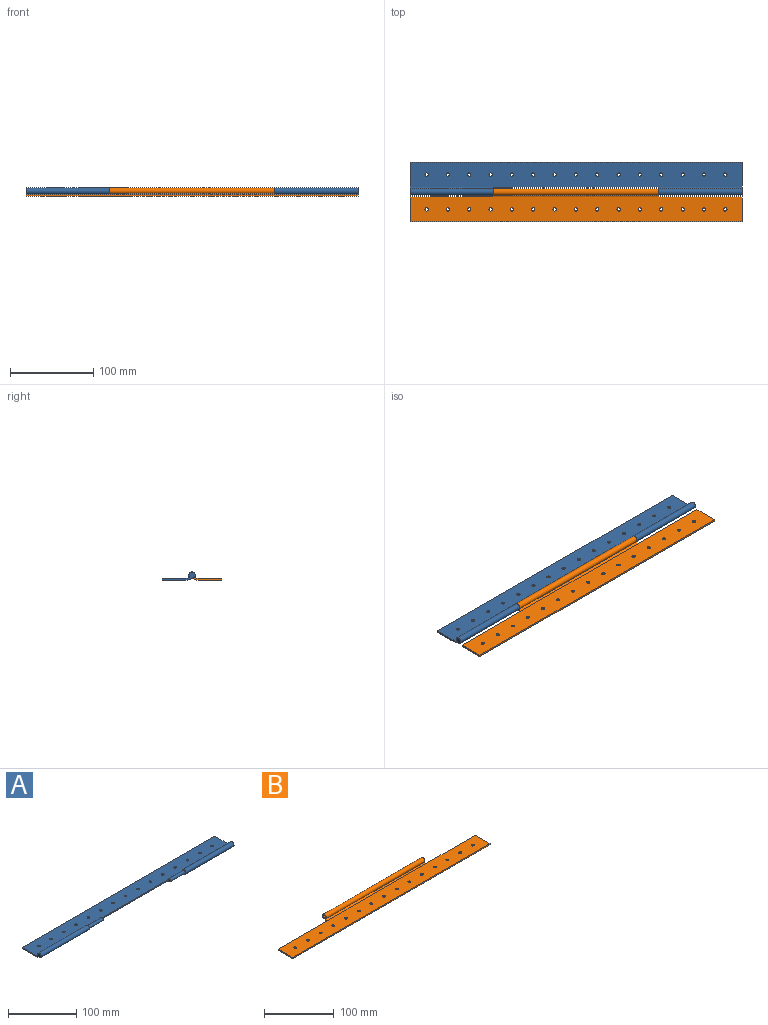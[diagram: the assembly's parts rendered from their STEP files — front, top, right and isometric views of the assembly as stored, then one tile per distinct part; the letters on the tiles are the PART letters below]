
ASSEMBLY  parts=2 mates=1
PART A: 33 faces, bbox 400x39.9x9.7 mm
  f0: cylinder r=3.86mm len=100mm, axis (1,0,0), area 2115.6mm2, adj f1,f2,f5,f6
  f1: plane 39.91x9.68mm, normal (-1,0,0), area 115.6mm2, adj f0,f5,f6,f15,f31,f32
  f2: plane 9.91x9.68mm, normal (1,0,0), area 36mm2, adj f0,f3,f5,f6,f7
  f3: cylinder r=2.5mm len=30mm, axis (-1,0,0), area 471.2mm2, adj f2,f4
  f4: plane 5x5mm, normal (1,0,0), area 19.6mm2, adj f3
  f5: plane 100x3.32mm, normal (0,0.31,0.95), area 349.9mm2, adj f0,f1,f2,f31
  f6: plane 100x6.1mm, normal (0,-0.31,-0.95), area 640.7mm2, adj f0,f1,f2,f32
  f7: plane 200x2mm, normal (0,-1,0), area 400mm2, adj f2,f9,f31,f32
  f8: cylinder r=3.86mm len=100mm, axis (1,0,0), area 2120.4mm2, adj f9,f10,f13,f14
  f9: plane 9.91x9.68mm, normal (-1,0,0), area 35.9mm2, adj f7,f8,f11,f13,f14
  f10: plane 39.91x9.68mm, normal (1,0,0), area 115.6mm2, adj f8,f13,f14,f15,f31,f32
  f11: cylinder r=2.5mm len=30mm, axis (1,0,0), area 471.2mm2, adj f9,f12
  f12: plane 5x5mm, normal (-1,0,0), area 19.6mm2, adj f11
  f13: plane 100x3.32mm, normal (0,0.31,0.95), area 349.9mm2, adj f8,f9,f10,f31
  f14: plane 100x6.05mm, normal (0,-0.31,-0.95), area 636.2mm2, adj f8,f9,f10,f32
  f15: plane 400x2mm, normal (0,1,0), area 800mm2, adj f1,f10,f31,f32
  f16: cylinder r=2mm len=4mm, axis (0,0,-1), area 25.1mm2, adj f31,f32
  f17: cylinder r=2mm len=4mm, axis (0,0,-1), area 25.1mm2, adj f31,f32
  f18: cylinder r=2mm len=4mm, axis (0,0,-1), area 25.1mm2, adj f31,f32
  f19: cylinder r=2mm len=4mm, axis (0,0,-1), area 25.1mm2, adj f31,f32
  f20: cylinder r=2mm len=4mm, axis (0,0,-1), area 25.1mm2, adj f31,f32
  f21: cylinder r=2mm len=4mm, axis (0,0,-1), area 25.1mm2, adj f31,f32
  f22: cylinder r=2mm len=4mm, axis (0,0,-1), area 25.1mm2, adj f31,f32
  f23: cylinder r=2mm len=4mm, axis (0,0,-1), area 25.1mm2, adj f31,f32
  f24: cylinder r=2mm len=4mm, axis (0,0,-1), area 25.1mm2, adj f31,f32
  f25: cylinder r=2mm len=4mm, axis (0,0,-1), area 25.1mm2, adj f31,f32
  f26: cylinder r=2mm len=4mm, axis (0,0,-1), area 25.1mm2, adj f31,f32
  f27: cylinder r=2mm len=4mm, axis (0,0,-1), area 25.1mm2, adj f31,f32
  f28: cylinder r=2mm len=4mm, axis (0,0,-1), area 25.1mm2, adj f31,f32
  f29: cylinder r=2mm len=4mm, axis (0,0,-1), area 25.1mm2, adj f31,f32
  f30: cylinder r=2mm len=4mm, axis (0,0,-1), area 25.1mm2, adj f31,f32
  f31: plane 400x30mm, normal (0,0,1), area 11811.5mm2, adj f1,f5,f7,f10,f13,f15,f16,f17
  f32: plane 400x30mm, normal (0,0,-1), area 11811.5mm2, adj f1,f6,f7,f10,f14,f15,f16,f17
PART B: 31 faces, bbox 400x39.8x9.7 mm
  f0: cylinder r=3.86mm len=200mm, axis (1,0,0), area 4250.2mm2, adj f1,f2,f5,f6
  f1: plane 9.81x9.68mm, normal (1,0,0), area 35.7mm2, adj f0,f3,f5,f6,f10
  f2: plane 9.81x9.68mm, normal (-1,0,0), area 35.7mm2, adj f0,f5,f6,f7,f29
  f3: cylinder r=2.5mm len=25mm, axis (1,0,0), area 392.7mm2, adj f1,f4
  f4: plane 5x5mm, normal (1,0,0), area 19.6mm2, adj f3
  f5: plane 200x3.22mm, normal (0,-0.32,0.95), area 681.2mm2, adj f0,f1,f2,f27
  f6: plane 200x5.9mm, normal (0,0.32,-0.95), area 1244.7mm2, adj f0,f1,f2,f28
  f7: plane 100x2mm, normal (0,1,0), area 200mm2, adj f2,f26,f27,f28
  f8: plane 400x2mm, normal (0,-1,0), area 800mm2, adj f9,f26,f27,f28
  f9: plane 30x2mm, normal (1,0,0), area 60mm2, adj f8,f10,f27,f28
  f10: plane 100x2mm, normal (0,1,0), area 200mm2, adj f1,f9,f27,f28
  f11: cylinder r=2mm len=4mm, axis (0,0,-1), area 25.1mm2, adj f27,f28
  f12: cylinder r=2mm len=4mm, axis (0,0,-1), area 25.1mm2, adj f27,f28
  f13: cylinder r=2mm len=4mm, axis (0,0,-1), area 25.1mm2, adj f27,f28
  f14: cylinder r=2mm len=4mm, axis (0,0,-1), area 25.1mm2, adj f27,f28
  f15: cylinder r=2mm len=4mm, axis (0,0,-1), area 25.1mm2, adj f27,f28
  f16: cylinder r=2mm len=4mm, axis (0,0,-1), area 25.1mm2, adj f27,f28
  f17: cylinder r=2mm len=4mm, axis (0,0,-1), area 25.1mm2, adj f27,f28
  f18: cylinder r=2mm len=4mm, axis (0,0,-1), area 25.1mm2, adj f27,f28
  f19: cylinder r=2mm len=4mm, axis (0,0,-1), area 25.1mm2, adj f27,f28
  f20: cylinder r=2mm len=4mm, axis (0,0,-1), area 25.1mm2, adj f27,f28
  f21: cylinder r=2mm len=4mm, axis (0,0,-1), area 25.1mm2, adj f27,f28
  f22: cylinder r=2mm len=4mm, axis (0,0,-1), area 25.1mm2, adj f27,f28
  f23: cylinder r=2mm len=4mm, axis (0,0,-1), area 25.1mm2, adj f27,f28
  f24: cylinder r=2mm len=4mm, axis (0,0,-1), area 25.1mm2, adj f27,f28
  f25: cylinder r=2mm len=4mm, axis (0,0,-1), area 25.1mm2, adj f27,f28
  f26: plane 30x2mm, normal (-1,0,0), area 60mm2, adj f7,f8,f27,f28
  f27: plane 400x30mm, normal (0,0,1), area 11811.5mm2, adj f5,f7,f8,f9,f10,f11,f12,f13
  f28: plane 400x30mm, normal (0,0,-1), area 11811.5mm2, adj f6,f7,f8,f9,f10,f11,f12,f13
  f29: cylinder r=2.5mm len=30mm, axis (-1,0,0), area 471.2mm2, adj f2,f30
  f30: plane 5x5mm, normal (-1,0,0), area 19.6mm2, adj f29
PLACE A t=(-123.85,-85.67,-33.15)mm
PLACE B t=(-123.85,-85.67,-33.15)mm fixed
MATE revolute A.f0 <-> B.f0  axis (1,0,0) through (-196.08,-91.72,-27.32)mm
